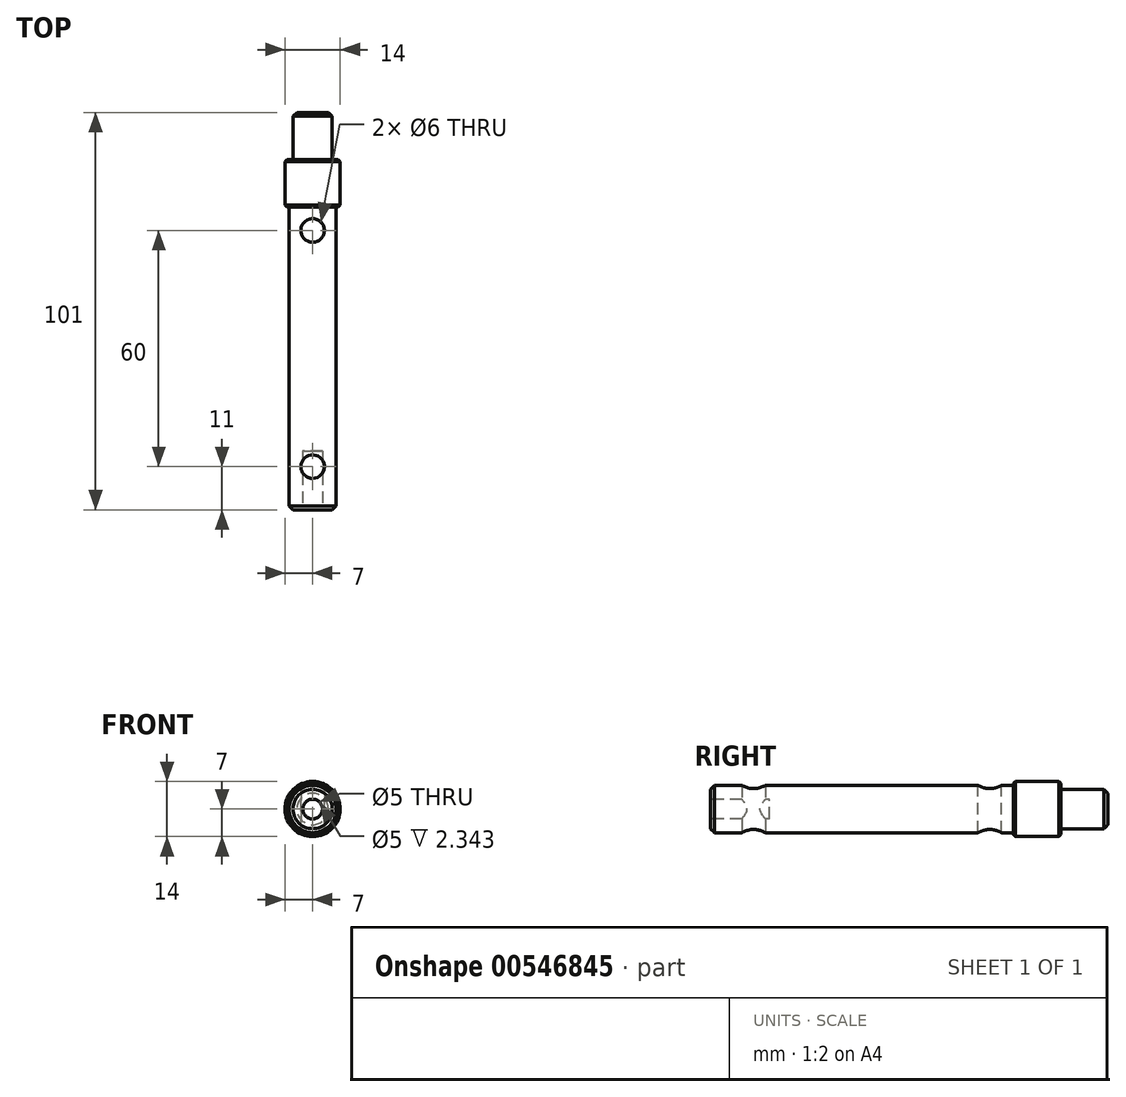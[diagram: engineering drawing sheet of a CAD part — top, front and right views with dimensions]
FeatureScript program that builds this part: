
annotation { "Feature Type Name" : "Feature", "Feature Type Description" : "" }
export const myFeature = defineFeature(function(context is Context, id is Id, definition is map)
    precondition{}
    {
        {
            var Q0;
            Q0=qCreatedBy(makeId("Front.planeOp"),FACE);
            var sketch = newSketch(context, id + "F0", { "sketchPlane" : qUnion([Q0])});
            skCircle(sketch, "E0", {"center": v(0, 0) * mm, "radius": 6 * mm});
            skCircle(sketch, "E1", {"center": v(0, 0) * mm, "radius": 5 * mm});
            skCircle(sketch, "E2", {"center": v(0, 0) * mm, "radius": 7 * mm});
            skSolve(sketch);
        }
        {
            var Q0;
            Q0=makeQuery(id+"F0.imprint","IMPRINT",FACE,{"disambiguationData":[TD([[makeQuery(id+"F0.imprint","IMPRINT",EDGE,{"derivedFrom":sQuery(id+"F0.wireOp",EDGE,"E0")}),-1.0]])]});
            extrude(context, id + "F1", {"entities" : qUnion([Q0]), "depth" : 12 * mm, "offsetDistance" : 25 * mm});
        }
        {
            var Q0;
            Q0=makeQuery(id+"F0.imprint","IMPRINT",FACE,{"disambiguationData":[TD([[makeQuery(id+"F0.imprint","IMPRINT",EDGE,{"derivedFrom":sQuery(id+"F0.wireOp",EDGE,"E0")}),1.0]])]});
            extrude(context, id + "F2", {"entities" : qUnion([Q0]), "operationType" : NewBodyOperationType.ADD, "depth" : 24 * mm, "offsetDistance" : 25 * mm});
        }
        {
            var Q0;
            Q0=makeQuery(id+"F0.imprint","IMPRINT",FACE,{"disambiguationData":[TD([[makeQuery(id+"F0.imprint","IMPRINT",EDGE,{"derivedFrom":sQuery(id+"F0.wireOp",EDGE,"E1")}),1.0]])]});
            extrude(context, id + "F3", {"entities" : qUnion([Q0]), "operationType" : NewBodyOperationType.ADD, "depth" : 24 * mm, "offsetDistance" : 25 * mm, "hasSecondDirection" : true, "secondDirectionOppositeDirection" : true, "secondDirectionDepth" : 12 * mm});
        }
        {
            var Q0;
            Q0=makeQuery(id+"F3.opExtrude","CAP_EDGE",EDGE,{"disambiguationData":[OSD([sQuery(id+"F0.wireOp",EDGE,"E1")])],"isStart":true});
            chamfer(context, id + "F4", {"entities" : qUnion([Q0]), "width" : 1 * mm, "tangentPropagation" : true});
        }
        {
            var Q0;
            Q0=makeQuery(id+"F2.opExtrude","CAP_EDGE",EDGE,{"disambiguationData":[OSD([sQuery(id+"F0.wireOp",EDGE,"E0")])],"isStart":false});
            var Q1;
            Q1=makeQuery(id+"F1.opExtrude","CAP_EDGE",EDGE,{"disambiguationData":[OSD([sQuery(id+"F0.wireOp",EDGE,"E2")])],"isStart":false});
            var Q2;
            Q2=makeQuery(id+"F1.opExtrude","SWEPT_FACE",FACE,{"disambiguationData":[OSD([sQuery(id+"F0.wireOp",EDGE,"E2")])]});
            chamfer(context, id + "F5", {"entities" : qUnion([Q0, Q1, Q2]), "width" : .5 * mm, "tangentPropagation" : true});
        }
        {
            var Q0;
            Q0=qCreatedBy(makeId("Top.planeOp"),FACE);
            var sketch = newSketch(context, id + "F6", { "sketchPlane" : qUnion([Q0])});
            skLineSegment(sketch, "E3", {"start": v(0, 0) * mm, "end": v(0, -18) * mm, "construction": true});
            skLineSegment(sketch, "E4", {"start": v(0, -18) * mm, "end": v(25, -18) * mm, "construction": true});
            skCircle(sketch, "E5", {"center": v(0, -18) * mm, "radius": 3 * mm});
            skLineSegment(sketch, "E6", {"start": v(0, -18) * mm, "end": v(0, -78) * mm, "construction": true});
            skLineSegment(sketch, "E7", {"start": v(0, -78) * mm, "end": v(25, -78) * mm, "construction": true});
            skCircle(sketch, "E8", {"center": v(0, -78) * mm, "radius": 3 * mm});
            skSolve(sketch);
        }
        {
            var Q0;
            Q0=qSketchRegion(id+"F6",true);
            extrude(context, id + "F7", {"entities" : qUnion([Q0]), "operationType" : NewBodyOperationType.REMOVE, "oppositeDirection" : true, "depth" : 25 * mm, "offsetDistance" : 25 * mm, "hasSecondDirection" : true, "secondDirectionOppositeDirection" : false, "secondDirectionDepth" : 25 * mm});
        }
        {
            var Q0;
            {var subQ0=sQuery(id+"F0.wireOp",EDGE,"E1");Q0=makeQuery(id+"F3.boolean.opBoolean","MERGE",FACE,{"derivedFrom":[makeQuery(id+"F2.opExtrude","CAP_FACE",FACE,{"disambiguationData":[OSD([sQuery(id+"F0.wireOp",EDGE,"E0"),subQ0])],"isStart":false}),makeQuery(id+"F3.opExtrude","CAP_FACE",FACE,{"disambiguationData":[OSD([subQ0])],"isStart":false})]});}
            cPlane(context, id + "F8", {"entities" : qUnion([Q0]), "cplaneType" : CPlaneType.OFFSET, "offset" : 25 * mm, "width" : 150 * mm, "height" : 150 * mm});
        }
        {
            var Q0;
            Q0=qCreatedBy(id+"F8.planeOp",FACE);
            var sketch = newSketch(context, id + "F9", { "sketchPlane" : qUnion([Q0])});
            skCircle(sketch, "E9", {"center": v(0, 0) * mm, "radius": 6 * mm});
            skSolve(sketch);
        }
        {
            var Q0;
            Q0=makeQuery(id+"F9.imprint","IMPRINT",FACE,{"disambiguationData":[TD([[makeQuery(id+"F9.imprint","IMPRINT",EDGE,{"derivedFrom":sQuery(id+"F9.wireOp",EDGE,"E9")}),1.0]])]});
            extrude(context, id + "F10", {"entities" : qUnion([Q0]), "operationType" : NewBodyOperationType.ADD, "oppositeDirection" : true, "depth" : 26 * mm, "offsetDistance" : 25 * mm, "hasSecondDirection" : true, "secondDirectionOppositeDirection" : false, "secondDirectionDepth" : 40 * mm});
        }
        {
            var Q0;
            Q0=makeQuery(id+"F10.opExtrude","CAP_EDGE",EDGE,{"disambiguationData":[OSD([sQuery(id+"F9.wireOp",EDGE,"E9")])],"isStart":true});
            chamfer(context, id + "F11", {"entities" : qUnion([Q0]), "width" : 1 * mm, "tangentPropagation" : true});
        }
        {
            var Q0;
            Q0 = qSketchRegion(id + "F6", true);
            extrude(context, id + "F12", {"entities" : qUnion([Q0]), "operationType" : NewBodyOperationType.REMOVE, "depth" : 25 * mm, "offsetDistance" : 25 * mm, "hasSecondDirection" : true, "secondDirectionOppositeDirection" : true, "secondDirectionDepth" : 25 * mm});
        }
        {
            var Q0;
            Q0=makeQuery(id+"F10.opExtrude","CAP_FACE",FACE,{"disambiguationData":[OSD([sQuery(id+"F9.wireOp",EDGE,"E9")])],"isStart":true});
            var sketch = newSketch(context, id + "F13", { "sketchPlane" : qUnion([Q0])});
            skCircle(sketch, "E10", {"center": v(0, 0) * mm, "radius": 2.5 * mm});
            skSolve(sketch);
        }
        {
            var Q0;
            Q0 = qSketchRegion(id + "F13", true);
            extrude(context, id + "F14", {"entities" : qUnion([Q0]), "operationType" : NewBodyOperationType.REMOVE, "oppositeDirection" : true, "depth" : 15 * mm, "offsetDistance" : 25 * mm});
        }
    });
